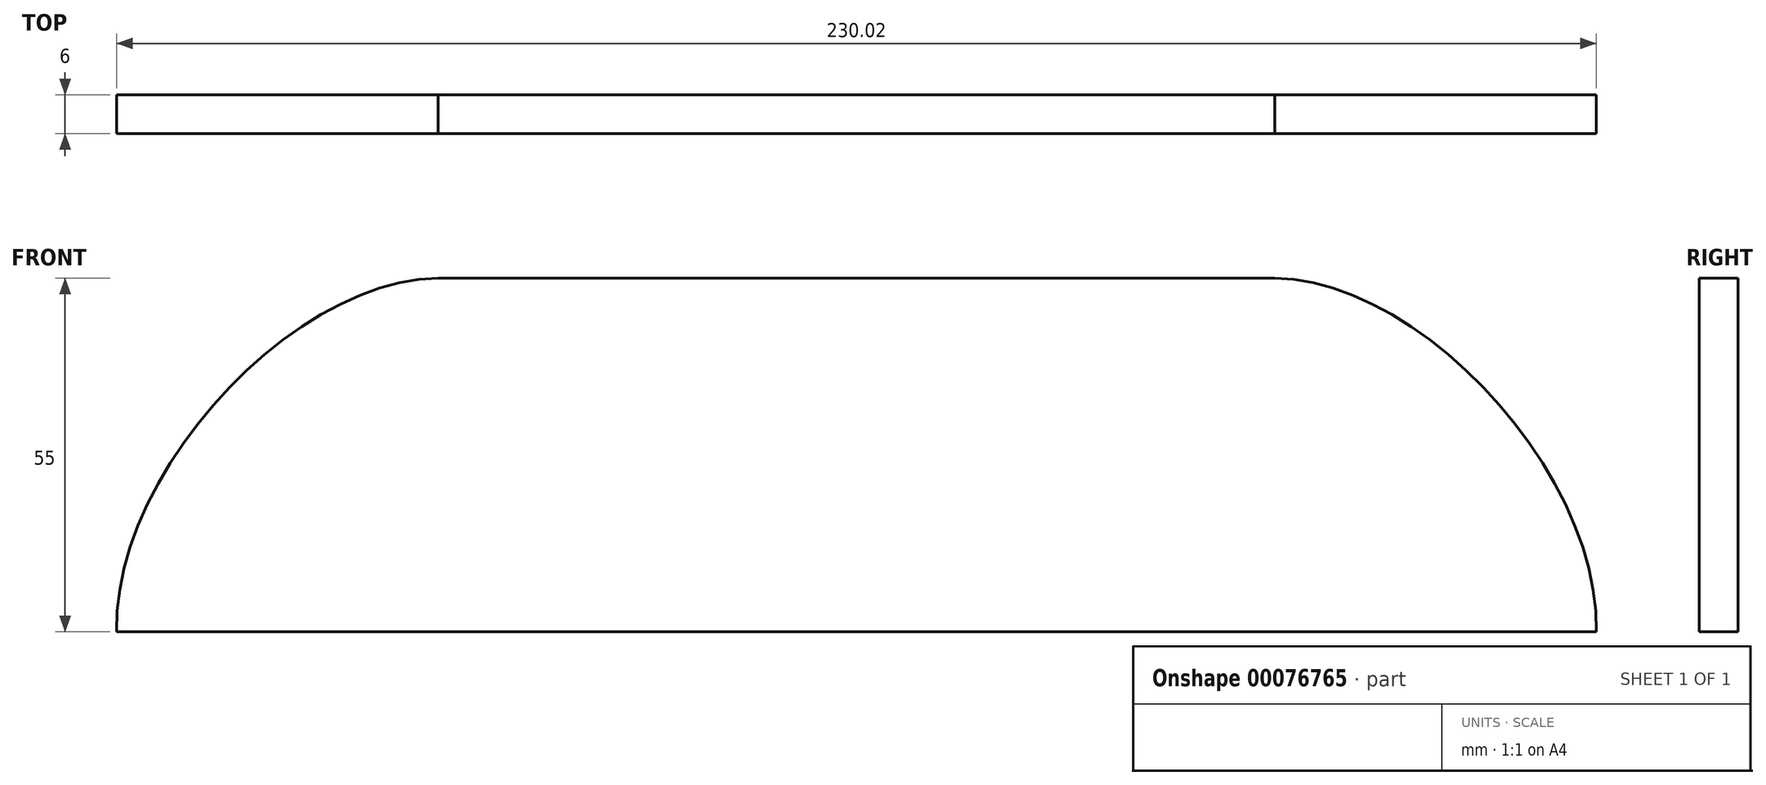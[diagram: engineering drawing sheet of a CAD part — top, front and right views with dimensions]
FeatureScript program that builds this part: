
annotation { "Feature Type Name" : "Feature", "Feature Type Description" : "" }
export const myFeature = defineFeature(function(context is Context, id is Id, definition is map)
    precondition{}
    {
        {
            var Q0;
            Q0=qCreatedBy(makeId("Front.planeOp"),FACE);
            var sketch = newSketch(context, id + "F0", { "sketchPlane" : qUnion([Q0])});
            skLineSegment(sketch, "E0", {"start": v(0, 0) * mm, "end": v(115, 0) * mm});
            skLineSegment(sketch, "E1", {"start": v(0, 55) * mm, "end": v(65, 55) * mm});
            skFitSpline(sketch, "E2", {"points": [v(65, 55) * mm, v(115, 0) * mm], "startDerivative": vector(68.16, -0.86) * mm, "endDerivative": vector(-1.55, -74.05) * mm});
            skLineSegment(sketch, "E3.MirrorCS", {"start": v(0, 55) * mm, "end": v(-65, 55) * mm});
            skLineSegment(sketch, "E4.MirrorCS", {"start": v(0, 0) * mm, "end": v(-115, 0) * mm});
            skFitSpline(sketch, "E5.MirrorCS", {"points": [v(-65, 55) * mm, v(-115, 0) * mm], "startDerivative": vector(-68.16, -0.86) * mm, "endDerivative": vector(1.55, -74.05) * mm});
            skSolve(sketch);
        }
        {
            var Q0;
            Q0=makeQuery(id+"F0.imprint","IMPRINT",FACE,{"disambiguationData":[TD([[makeQuery(id+"F0.imprint","IMPRINT",EDGE,{"derivedFrom":sQuery(id+"F0.wireOp",EDGE,"E0")}),1.0]])]});
            extrude(context, id + "F1", {"entities" : qUnion([Q0]), "depth" : 6 * mm});
        }
    });
